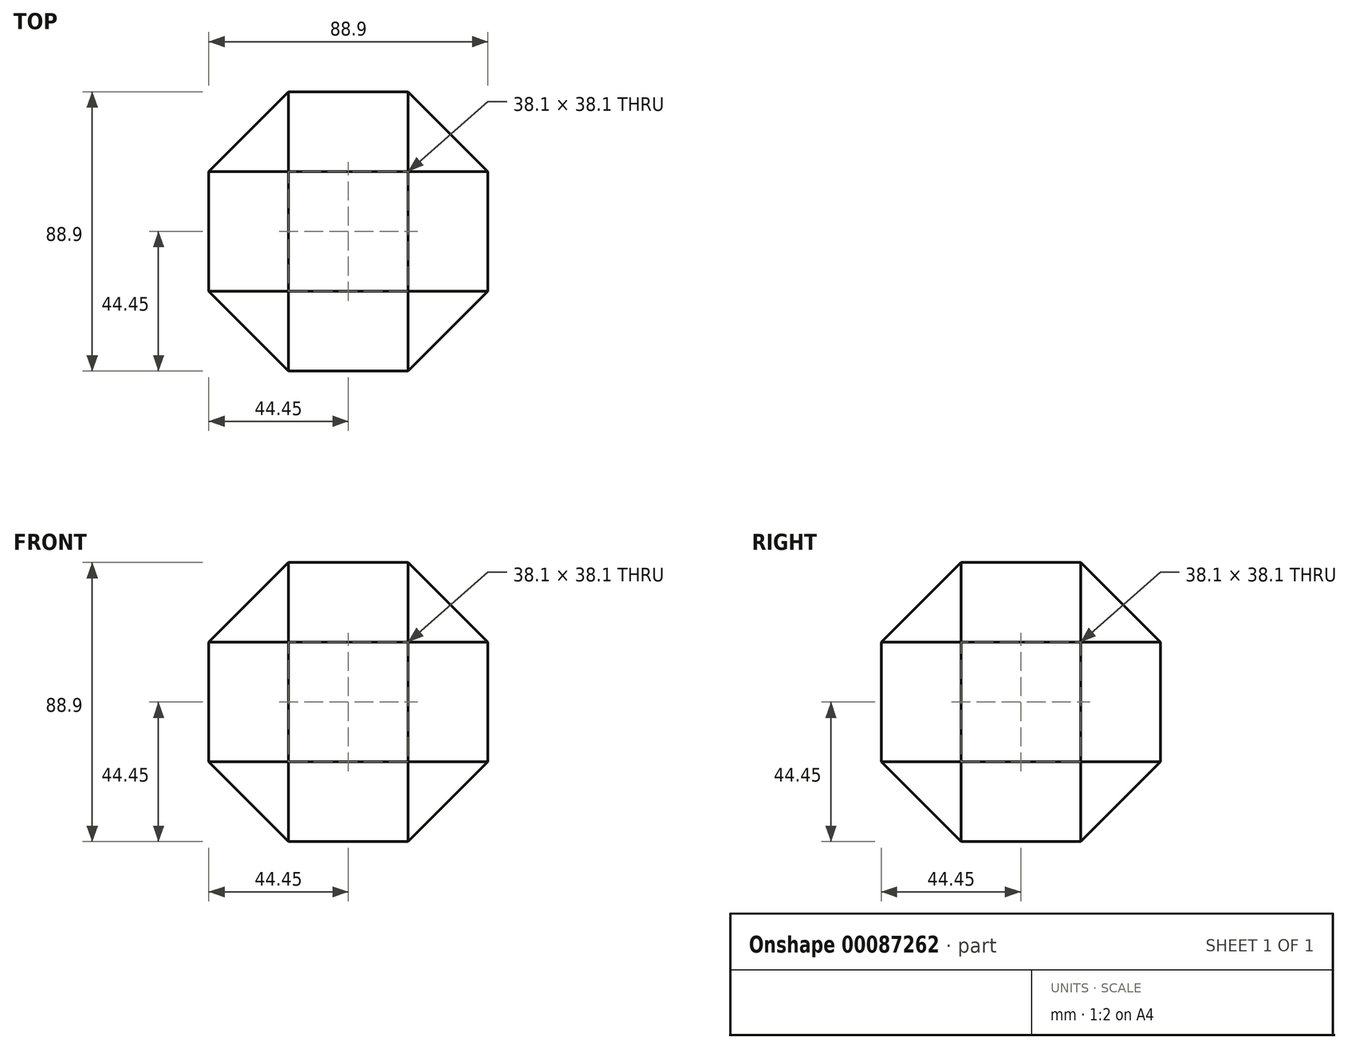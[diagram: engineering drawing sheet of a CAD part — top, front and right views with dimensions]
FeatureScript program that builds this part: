
annotation { "Feature Type Name" : "Feature", "Feature Type Description" : "" }
export const myFeature = defineFeature(function(context is Context, id is Id, definition is map)
    precondition{}
    {
        {
            var Q0;
            Q0=qCreatedBy(makeId("Front.planeOp"),FACE);
            var sketch = newSketch(context, id + "F0", { "sketchPlane" : qUnion([Q0])});
            skLineSegment(sketch, "E0.bottom", {"start": v(-19.05, 44.45) * mm, "end": v(19.05, 44.45) * mm});
            skLineSegment(sketch, "E0.top", {"start": v(-19.05, -44.45) * mm, "end": v(19.05, -44.45) * mm});
            skLineSegment(sketch, "E0.left", {"start": v(-19.05, 44.45) * mm, "end": v(-19.05, -44.45) * mm});
            skLineSegment(sketch, "E0.right", {"start": v(19.05, 44.45) * mm, "end": v(19.05, -44.45) * mm});
            skPoint(sketch, "E0.middle", {"position": v(0, 0) * mm});
            skLineSegment(sketch, "E1.bottom", {"start": v(-44.45, 19.05) * mm, "end": v(44.45, 19.05) * mm});
            skLineSegment(sketch, "E1.top", {"start": v(-44.45, -19.05) * mm, "end": v(44.45, -19.05) * mm});
            skLineSegment(sketch, "E1.left", {"start": v(-44.45, 19.05) * mm, "end": v(-44.45, -19.05) * mm});
            skLineSegment(sketch, "E1.right", {"start": v(44.45, 19.05) * mm, "end": v(44.45, -19.05) * mm});
            skLineSegment(sketch, "E2", {"start": v(-19.05, 44.45) * mm, "end": v(-44.45, 19.05) * mm});
            skLineSegment(sketch, "E3", {"start": v(-44.45, -19.05) * mm, "end": v(-19.05, -44.45) * mm});
            skLineSegment(sketch, "E4", {"start": v(19.05, -44.45) * mm, "end": v(44.45, -19.05) * mm});
            skLineSegment(sketch, "E5", {"start": v(44.45, 19.05) * mm, "end": v(19.05, 44.45) * mm});
            skSolve(sketch);
        }
        {
            var Q0;
            Q0=qCreatedBy(makeId("Right.planeOp"),FACE);
            var sketch = newSketch(context, id + "F1", { "sketchPlane" : qUnion([Q0])});
            skLineSegment(sketch, "E6.bottom", {"start": v(19.05, 44.45) * mm, "end": v(-19.05, 44.45) * mm});
            skLineSegment(sketch, "E6.top", {"start": v(19.05, -44.45) * mm, "end": v(-19.05, -44.45) * mm});
            skLineSegment(sketch, "E6.left", {"start": v(19.05, 44.45) * mm, "end": v(19.05, -44.45) * mm});
            skLineSegment(sketch, "E6.right", {"start": v(-19.05, 44.45) * mm, "end": v(-19.05, -44.45) * mm});
            skPoint(sketch, "E6.middle", {"position": v(0, 0) * mm});
            skLineSegment(sketch, "E7.bottom", {"start": v(44.45, 19.05) * mm, "end": v(-44.45, 19.05) * mm});
            skLineSegment(sketch, "E7.top", {"start": v(44.45, -19.05) * mm, "end": v(-44.45, -19.05) * mm});
            skLineSegment(sketch, "E7.left", {"start": v(44.45, 19.05) * mm, "end": v(44.45, -19.05) * mm});
            skLineSegment(sketch, "E7.right", {"start": v(-44.45, 19.05) * mm, "end": v(-44.45, -19.05) * mm});
            skLineSegment(sketch, "E8", {"start": v(44.45, 19.05) * mm, "end": v(19.05, 44.45) * mm});
            skLineSegment(sketch, "E9", {"start": v(-19.05, 44.45) * mm, "end": v(-44.45, 19.05) * mm});
            skLineSegment(sketch, "E10", {"start": v(-44.45, -19.05) * mm, "end": v(-19.05, -44.45) * mm});
            skLineSegment(sketch, "E11", {"start": v(19.05, -44.45) * mm, "end": v(44.45, -19.05) * mm});
            skSolve(sketch);
        }
        {
            var Q0;
            Q0=qCreatedBy(makeId("Top.planeOp"),FACE);
            var sketch = newSketch(context, id + "F2", { "sketchPlane" : qUnion([Q0])});
            skLineSegment(sketch, "E12.bottom", {"start": v(-19.05, -44.45) * mm, "end": v(19.05, -44.45) * mm});
            skLineSegment(sketch, "E12.top", {"start": v(-19.05, 44.45) * mm, "end": v(19.05, 44.45) * mm});
            skLineSegment(sketch, "E12.left", {"start": v(-19.05, -44.45) * mm, "end": v(-19.05, 44.45) * mm});
            skLineSegment(sketch, "E12.right", {"start": v(19.05, -44.45) * mm, "end": v(19.05, 44.45) * mm});
            skPoint(sketch, "E12.middle", {"position": v(0, 0) * mm});
            skLineSegment(sketch, "E13.bottom", {"start": v(-44.45, -19.05) * mm, "end": v(44.45, -19.05) * mm});
            skLineSegment(sketch, "E13.top", {"start": v(-44.45, 19.05) * mm, "end": v(44.45, 19.05) * mm});
            skLineSegment(sketch, "E13.left", {"start": v(-44.45, -19.05) * mm, "end": v(-44.45, 19.05) * mm});
            skLineSegment(sketch, "E13.right", {"start": v(44.45, -19.05) * mm, "end": v(44.45, 19.05) * mm});
            skLineSegment(sketch, "E14", {"start": v(-19.05, 44.45) * mm, "end": v(-44.45, 19.05) * mm});
            skLineSegment(sketch, "E15", {"start": v(-44.45, -19.05) * mm, "end": v(-19.05, -44.45) * mm});
            skLineSegment(sketch, "E16", {"start": v(19.05, -44.45) * mm, "end": v(44.45, -19.05) * mm});
            skLineSegment(sketch, "E17", {"start": v(44.45, 19.05) * mm, "end": v(19.05, 44.45) * mm});
            skSolve(sketch);
        }
        {
            var Q0;
            Q0 = qSketchRegion(id + "F0", true);
            extrude(context, id + "F3", {"entities" : qUnion([Q0]), "endBound" : BoundingType.SYMMETRIC, "depth" : 38.1 * mm, "hasSecondDirection" : true, "secondDirectionOppositeDirection" : true, "secondDirectionDepth" : 25.4 * mm});
        }
        {
            var Q0;
            Q0 = qSketchRegion(id + "F1", true);
            extrude(context, id + "F4", {"entities" : qUnion([Q0]), "endBound" : BoundingType.SYMMETRIC, "depth" : 38.1 * mm});
        }
        {
            var Q0;
            Q0 = qSketchRegion(id + "F2", true);
            extrude(context, id + "F5", {"entities" : qUnion([Q0]), "endBound" : BoundingType.SYMMETRIC, "depth" : 38.1 * mm});
        }
    });
